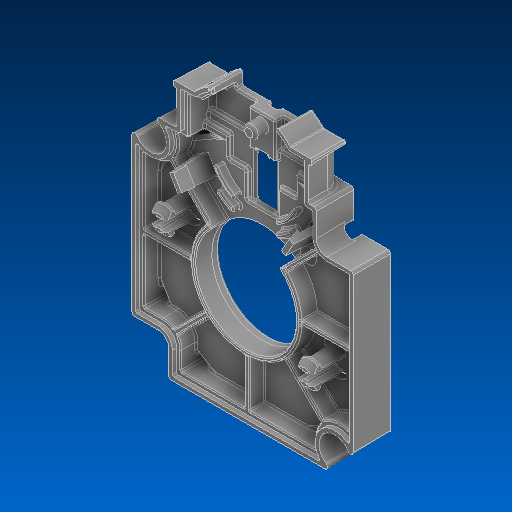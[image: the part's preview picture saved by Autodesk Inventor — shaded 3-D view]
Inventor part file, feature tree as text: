
AUTODESK INVENTOR PART (.ipt)
format: ipt  version: 2022.2 (Build 262287000, 287)  size: 1,838,592 bytes
history: native  units: in
note: dims shown in document units (in); Inventor stores cm internally (conversion verified against a paired STEP export)
features: fillet x1
ambient origin geometry x8: Origin, YZ Plane, XZ Plane, XY Plane, X Axis, Y Axis, Z Axis, Center Point
bodies: Solid1 (feature_tree)
feature tree (1):
  fillet  "Fillet32"  [1 undecoded]
note: 1 required parameter value undecoded (feature->parameter linkage not recoverable at this tier; creation-order binding heuristic only, values carry confidence <= 0.55)
